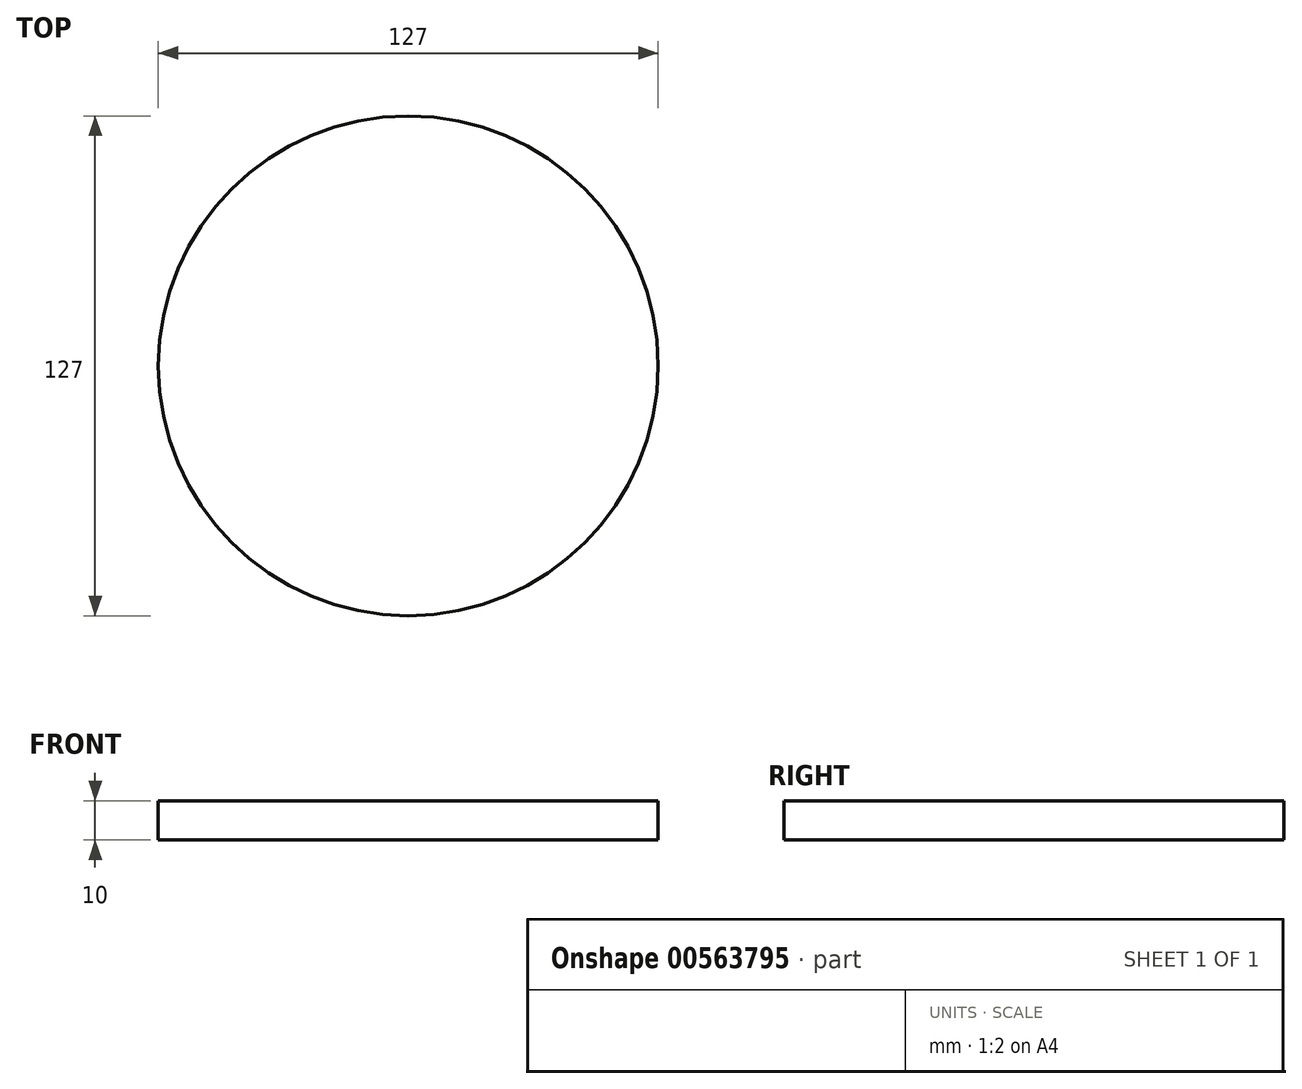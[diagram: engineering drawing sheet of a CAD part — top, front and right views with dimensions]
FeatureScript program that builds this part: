
annotation { "Feature Type Name" : "Feature", "Feature Type Description" : "" }
export const myFeature = defineFeature(function(context is Context, id is Id, definition is map)
    precondition{}
    {
        {
            var Q0;
            Q0=qCreatedBy(makeId("Top.planeOp"),FACE);
            var sketch = newSketch(context, id + "F0", { "sketchPlane" : qUnion([Q0])});
            skCircle(sketch, "E0", {"center": v(0, 0) * mm, "radius": 63.5 * mm});
            skSolve(sketch);
        }
        {
            var Q0;
            Q0=makeQuery(id+"F0.imprint","IMPRINT",FACE,{"disambiguationData":[TD([[makeQuery(id+"F0.imprint","IMPRINT",EDGE,{"derivedFrom":sQuery(id+"F0.wireOp",EDGE,"E0")}),1.0]])]});
            extrude(context, id + "F1", {"entities" : qUnion([Q0]), "depth" : 10 * mm, "offsetDistance" : 25.4 * mm});
        }
    });
